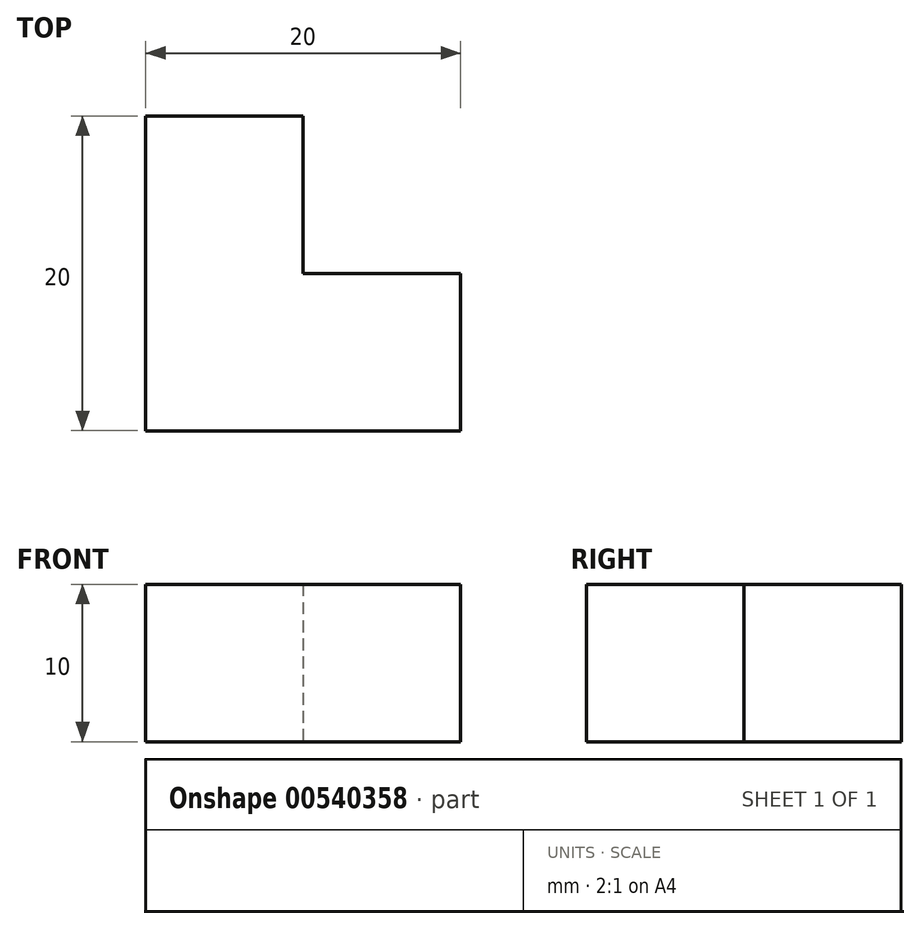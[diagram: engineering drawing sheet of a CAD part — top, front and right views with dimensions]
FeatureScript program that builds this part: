
annotation { "Feature Type Name" : "Feature", "Feature Type Description" : "" }
export const myFeature = defineFeature(function(context is Context, id is Id, definition is map)
    precondition{}
    {
        {
            var Q0;
            Q0=qCreatedBy(makeId("Top.planeOp"),FACE);
            var sketch = newSketch(context, id + "F0", { "sketchPlane" : qUnion([Q0])});
            skLineSegment(sketch, "E0", {"start": v(-20.42, 15.05) * mm, "end": v(-20.42, -4.95) * mm});
            skLineSegment(sketch, "E1", {"start": v(-20.42, -4.95) * mm, "end": v(-0.42, -4.95) * mm});
            skLineSegment(sketch, "E2", {"start": v(-0.42, -4.95) * mm, "end": v(-0.42, 5.05) * mm});
            skLineSegment(sketch, "E3", {"start": v(-0.42, 5.05) * mm, "end": v(-10.42, 5.05) * mm});
            skLineSegment(sketch, "E4", {"start": v(-10.42, 5.05) * mm, "end": v(-10.42, 15.05) * mm});
            skLineSegment(sketch, "E5", {"start": v(-10.42, 15.05) * mm, "end": v(-20.42, 15.05) * mm});
            skSolve(sketch);
        }
        {
            var Q0;
            Q0 = qSketchRegion(id + "F0", true);
            extrude(context, id + "F1", {"entities" : qUnion([Q0]), "depth" : 10 * mm, "offsetDistance" : 25 * mm});
        }
    });
